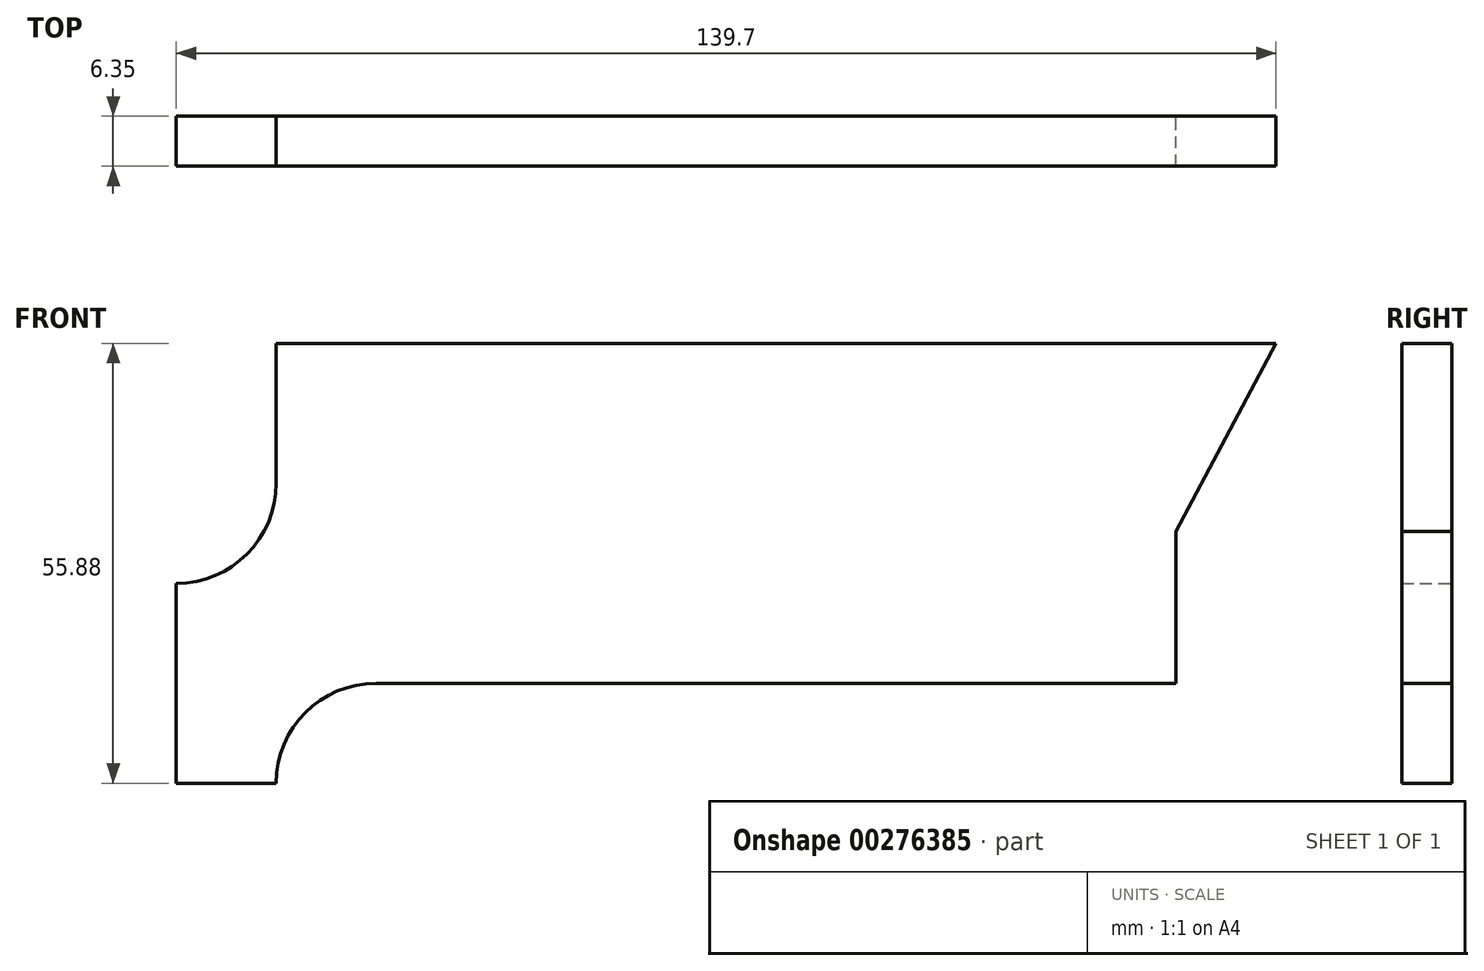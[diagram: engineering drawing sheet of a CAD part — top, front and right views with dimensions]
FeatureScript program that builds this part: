
annotation { "Feature Type Name" : "Feature", "Feature Type Description" : "" }
export const myFeature = defineFeature(function(context is Context, id is Id, definition is map)
    precondition{}
    {
        {
            var Q0;
            Q0=qCreatedBy(makeId("Front.planeOp"),FACE);
            var sketch = newSketch(context, id + "F0", { "sketchPlane" : qUnion([Q0])});
            skLineSegment(sketch, "E0.bottom", {"start": v(-24.45, 17.78) * mm, "end": v(102.55, 17.78) * mm});
            skLineSegment(sketch, "E0.top", {"start": v(-37.15, -38.1) * mm, "end": v(-24.45, -38.1) * mm});
            skLineSegment(sketch, "E0.left", {"start": v(-37.15, -12.7) * mm, "end": v(-37.15, -38.1) * mm});
            skLineSegment(sketch, "E1", {"start": v(102.55, 17.78) * mm, "end": v(89.85, -6.1) * mm});
            skLineSegment(sketch, "E2", {"start": v(89.85, -25.4) * mm, "end": v(89.85, -6.1) * mm});
            skArc(sketch, "E3", {"start": v(-11.75, -25.4) * mm, "mid": v(-20.73, -29.12) * mm, "end": v(-24.45, -38.1) * mm});
            skLineSegment(sketch, "E4", {"start": v(-37.15, -38.1) * mm, "end": v(-37.15, -12.7) * mm});
            skArc(sketch, "E5", {"start": v(-37.15, -12.7) * mm, "mid": v(-28.17, -8.98) * mm, "end": v(-24.45, 0) * mm});
            skLineSegment(sketch, "E6", {"start": v(-24.45, 17.78) * mm, "end": v(-24.45, 0) * mm});
            skPoint(sketch, "E7.orphan", {"position": v(-37.15, 17.78) * mm});
            skLineSegment(sketch, "E8", {"start": v(-11.75, -25.4) * mm, "end": v(89.85, -25.4) * mm});
            skSolve(sketch);
        }
        {
            var Q0;
            Q0 = qSketchRegion(id + "F0", true);
            extrude(context, id + "F1", {"entities" : qUnion([Q0]), "depth" : 6.35 * mm});
        }
    });
